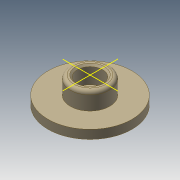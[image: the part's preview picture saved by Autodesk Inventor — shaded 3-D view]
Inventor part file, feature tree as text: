
AUTODESK INVENTOR PART (.ipt)
format: ipt  version: 2020.3 (Build 243373000, 373)  size: 127,488 bytes
history: native  units: in
note: dims shown in document units (in); Inventor stores cm internally (conversion verified against a paired STEP export)
features: sketch x4, extrude x2, hole x1, chamfer x1, fillet x1
ambient origin geometry x8: Origin, YZ Plane, XZ Plane, XY Plane, X Axis, Y Axis, Z Axis, Center Point
bodies: Solid1 (feature_tree)
feature tree (9):
  extrude  "Extrusion1"  Depth=0.75in TaperAngle=0.0deg
  sketch  "Sketch2"  dims[d3=0.25in d4=0.75in d5=0.72in d6=0.5in d7=90.0deg d8=1.0in d9=0.8108in d10=0.05in d11=0.125in d12=45.0deg]
  hole  "Hole1"  [1 undecoded]
  chamfer  "Chamfer1"  Distance=0.25in
  fillet  "Fillet1"  [1 undecoded]
  extrude  "Extrusion2"  [1 undecoded]
  sketch  "Sketch1"  dims[d0=1.125in d1=0.75in d2=0.0in]
  sketch  "Sketch3"  dims[d13=0.1in]
  sketch  "Sketch4"  dims[d14=2.4in d15=0.25in d16=0.0in]
note: 3 required parameter values undecoded (feature->parameter linkage not recoverable at this tier; creation-order binding heuristic only, values carry confidence <= 0.55)
